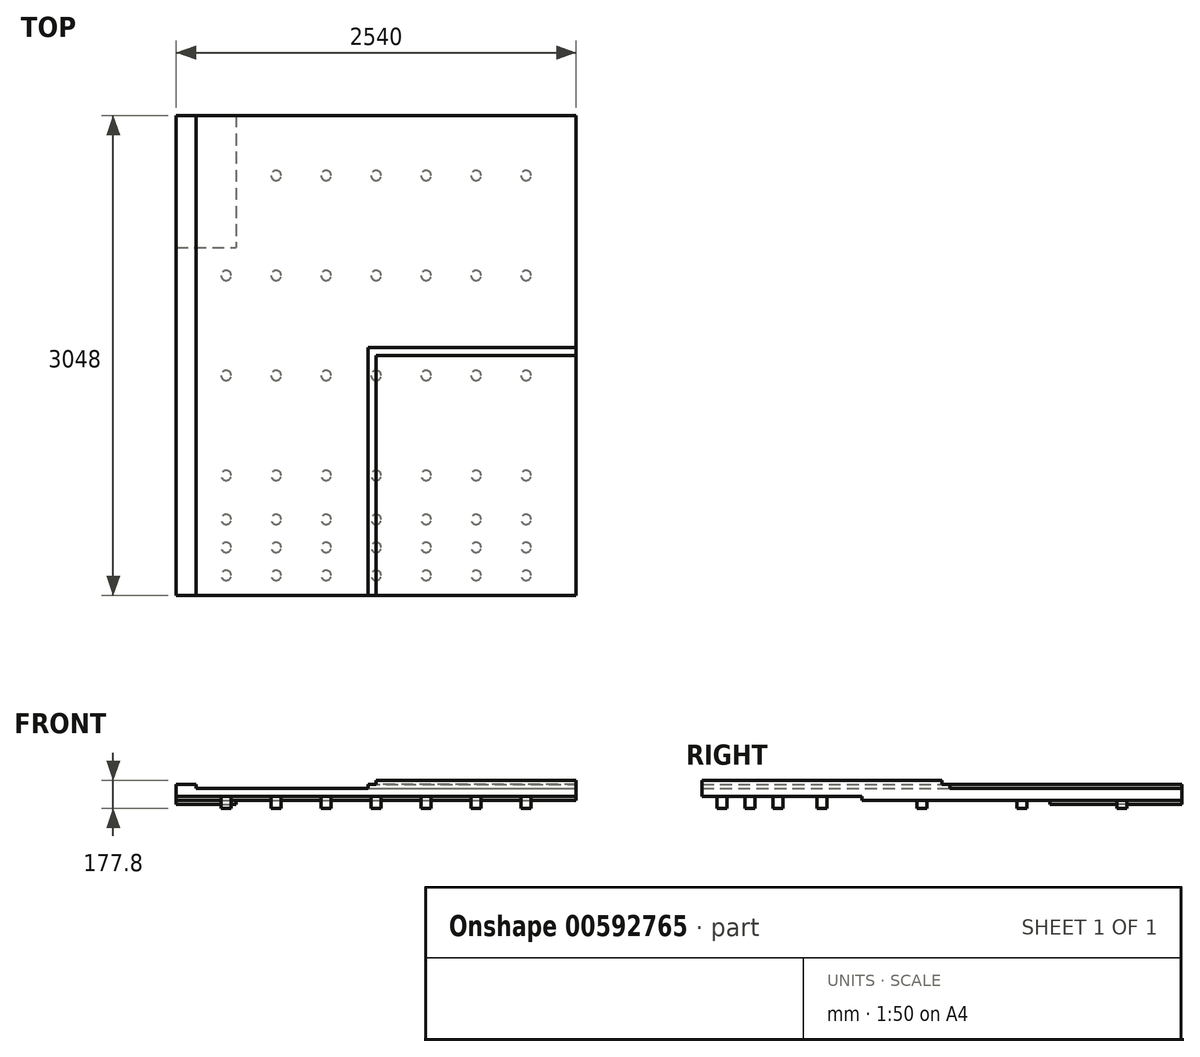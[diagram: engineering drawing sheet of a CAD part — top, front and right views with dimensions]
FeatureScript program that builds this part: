
annotation { "Feature Type Name" : "Feature", "Feature Type Description" : "" }
export const myFeature = defineFeature(function(context is Context, id is Id, definition is map)
    precondition{}
    {
        {
            var Q0;
            Q0=qCreatedBy(makeId("Top.planeOp"),FACE);
            var sketch = newSketch(context, id + "F0", { "sketchPlane" : qUnion([Q0])});
            skLineSegment(sketch, "E0.bottom", {"start": v(0, 0) * mm, "end": v(2540, 0) * mm});
            skLineSegment(sketch, "E0.top", {"start": v(0, 3048) * mm, "end": v(2540, 3048) * mm});
            skLineSegment(sketch, "E0.left", {"start": v(0, 0) * mm, "end": v(0, 3048) * mm});
            skLineSegment(sketch, "E0.right", {"start": v(2540, 0) * mm, "end": v(2540, 3048) * mm});
            skSolve(sketch);
        }
        {
            var Q0;
            Q0 = qSketchRegion(id + "F0", true);
            extrude(context, id + "F1", {"entities" : qUnion([Q0]), "depth" : 25.4 * mm, "offsetDistance" : 25.4 * mm});
        }
        {
            var Q0;
            Q0=makeQuery(id+"F1.opExtrude","CAP_FACE",FACE,{"disambiguationData":[OSD([sQuery(id+"F0.wireOp",EDGE,"E0.bottom"),sQuery(id+"F0.wireOp",EDGE,"E0.top"),sQuery(id+"F0.wireOp",EDGE,"E0.left"),sQuery(id+"F0.wireOp",EDGE,"E0.right")])],"isStart":false});
            extrude(context, id + "F2", {"entities" : qUnion([Q0]), "operationType" : NewBodyOperationType.ADD, "depth" : 25.4 * mm, "offsetDistance" : 25.4 * mm});
        }
        {
            var Q0;
            Q0=makeQuery(id+"F2.opExtrude","CAP_FACE",FACE,{"disambiguationData":[OSD([sQuery(id+"F0.wireOp",EDGE,"E0.bottom"),sQuery(id+"F0.wireOp",EDGE,"E0.top"),sQuery(id+"F0.wireOp",EDGE,"E0.left"),sQuery(id+"F0.wireOp",EDGE,"E0.right")])],"isStart":false});
            var sketch = newSketch(context, id + "F3", { "sketchPlane" : qUnion([Q0])});
            skLineSegment(sketch, "E1.bottom", {"start": v(1219.2, 0) * mm, "end": v(2540, 0) * mm});
            skLineSegment(sketch, "E1.top", {"start": v(1219.2, 1574.8) * mm, "end": v(2540, 1574.8) * mm});
            skLineSegment(sketch, "E1.left", {"start": v(1219.2, 0) * mm, "end": v(1219.2, 1574.8) * mm});
            skLineSegment(sketch, "E1.right", {"start": v(2540, 0) * mm, "end": v(2540, 1574.8) * mm});
            skLineSegment(sketch, "E2.bottom", {"start": v(0, 2032) * mm, "end": v(127, 2032) * mm});
            skLineSegment(sketch, "E2.top", {"start": v(0, 3048) * mm, "end": v(127, 3048) * mm});
            skLineSegment(sketch, "E2.left", {"start": v(0, 2032) * mm, "end": v(0, 3048) * mm});
            skLineSegment(sketch, "E2.right", {"start": v(127, 2032) * mm, "end": v(127, 3048) * mm});
            skLineSegment(sketch, "E3.bottom", {"start": v(0, 0) * mm, "end": v(127, 0) * mm});
            skLineSegment(sketch, "E3.left", {"start": v(0, 0) * mm, "end": v(0, 2032) * mm});
            skLineSegment(sketch, "E3.right", {"start": v(127, 0) * mm, "end": v(127, 2032) * mm});
            skSolve(sketch);
        }
        {
            var Q0;
            Q0=makeQuery(id+"F3.imprint","IMPRINT",FACE,{"disambiguationData":[TD([[makeQuery(id+"F3.imprint","IMPRINT",EDGE,{"derivedFrom":sQuery(id+"F3.wireOp",EDGE,"E2.top")}),-1.0]])]});
            var Q1;
            Q1=makeQuery(id+"F3.imprint","IMPRINT",FACE,{"disambiguationData":[TD([[makeQuery(id+"F3.imprint","IMPRINT",EDGE,{"derivedFrom":sQuery(id+"F3.wireOp",EDGE,"E3.bottom")}),1.0]])]});
            var Q2;
            Q2=makeQuery(id+"F3.imprint","IMPRINT",FACE,{"disambiguationData":[TD([[makeQuery(id+"F3.imprint","IMPRINT",EDGE,{"derivedFrom":sQuery(id+"F3.wireOp",EDGE,"E1.bottom")}),1.0]])]});
            extrude(context, id + "F4", {"entities" : qUnion([Q0, Q1, Q2]), "operationType" : NewBodyOperationType.ADD, "depth" : 25.4 * mm, "offsetDistance" : 25.4 * mm});
        }
        {
            var Q0;
            Q0=makeQuery(id+"F1.opExtrude","CAP_FACE",FACE,{"disambiguationData":[OSD([sQuery(id+"F0.wireOp",EDGE,"E0.bottom"),sQuery(id+"F0.wireOp",EDGE,"E0.top"),sQuery(id+"F0.wireOp",EDGE,"E0.left"),sQuery(id+"F0.wireOp",EDGE,"E0.right")])],"isStart":true});
            var sketch = newSketch(context, id + "F5", { "sketchPlane" : qUnion([Q0])});
            skLineSegment(sketch, "E4.bottom", {"start": v(0, -3048) * mm, "end": v(2540, -3048) * mm});
            skLineSegment(sketch, "E4.top", {"start": v(0, -1016) * mm, "end": v(2540, -1016) * mm});
            skLineSegment(sketch, "E4.left", {"start": v(0, -3048) * mm, "end": v(0, -1016) * mm});
            skLineSegment(sketch, "E4.right", {"start": v(2540, -3048) * mm, "end": v(2540, -1016) * mm});
            skSolve(sketch);
        }
        {
            var Q0;
            Q0 = qSketchRegion(id + "F5", true);
            var Q1;
            Q1=makeQuery(id+"F5.imprint","IMPRINT",FACE,{"disambiguationData":[TD([[makeQuery(id+"F5.imprint","IMPRINT",EDGE,{"derivedFrom":sQuery(id+"F5.wireOp",EDGE,"E4.bottom")}),1.0]])]});
            extrude(context, id + "F6", {"entities" : qUnion([Q0, Q1]), "operationType" : NewBodyOperationType.ADD, "depth" : 25.4 * mm, "offsetDistance" : 25.4 * mm});
        }
        {
            var Q0;
            Q0=makeQuery(id+"F6.opExtrude","CAP_FACE",FACE,{"disambiguationData":[OSD([sQuery(id+"F5.wireOp",EDGE,"E4.bottom"),sQuery(id+"F5.wireOp",EDGE,"E4.top"),sQuery(id+"F5.wireOp",EDGE,"E4.left"),sQuery(id+"F5.wireOp",EDGE,"E4.right")])],"isStart":false});
            var sketch = newSketch(context, id + "F7", { "sketchPlane" : qUnion([Q0])});
            skLineSegment(sketch, "E5.bottom", {"start": v(0, -3048) * mm, "end": v(381, -3048) * mm});
            skLineSegment(sketch, "E5.top", {"start": v(0, -2209.8) * mm, "end": v(381, -2209.8) * mm});
            skLineSegment(sketch, "E5.left", {"start": v(0, -3048) * mm, "end": v(0, -2209.8) * mm});
            skLineSegment(sketch, "E5.right", {"start": v(381, -3048) * mm, "end": v(381, -2209.8) * mm});
            skSolve(sketch);
        }
        {
            var Q0;
            Q0 = qSketchRegion(id + "F7", true);
            var Q1;
            Q1=makeQuery(id+"F7.imprint","IMPRINT",FACE,{"disambiguationData":[TD([[makeQuery(id+"F7.imprint","IMPRINT",EDGE,{"derivedFrom":sQuery(id+"F7.wireOp",EDGE,"E5.bottom")}),1.0]])]});
            extrude(context, id + "F8", {"entities" : qUnion([Q0, Q1]), "operationType" : NewBodyOperationType.ADD, "depth" : 25.4 * mm, "offsetDistance" : 25.4 * mm});
        }
        {
            var Q0;
            Q0=makeQuery(id+"F4.opExtrude","CAP_FACE",FACE,{"disambiguationData":[OSD([sQuery(id+"F3.wireOp",EDGE,"E1.bottom"),sQuery(id+"F3.wireOp",EDGE,"E1.top"),sQuery(id+"F3.wireOp",EDGE,"E1.left"),sQuery(id+"F3.wireOp",EDGE,"E1.right")])],"isStart":false});
            var sketch = newSketch(context, id + "F9", { "sketchPlane" : qUnion([Q0])});
            skLineSegment(sketch, "E6.bottom", {"start": v(2540, 0) * mm, "end": v(1270, 0) * mm});
            skLineSegment(sketch, "E6.top", {"start": v(2540, 1524) * mm, "end": v(1270, 1524) * mm});
            skLineSegment(sketch, "E6.left", {"start": v(2540, 0) * mm, "end": v(2540, 1524) * mm});
            skLineSegment(sketch, "E6.right", {"start": v(1270, 0) * mm, "end": v(1270, 1524) * mm});
            skSolve(sketch);
        }
        {
            var Q0;
            Q0=makeQuery(id+"F9.imprint","IMPRINT",FACE,{"disambiguationData":[TD([[makeQuery(id+"F9.imprint","IMPRINT",EDGE,{"derivedFrom":sQuery(id+"F9.wireOp",EDGE,"E6.bottom")}),1.0]])]});
            extrude(context, id + "F10", {"entities" : qUnion([Q0]), "operationType" : NewBodyOperationType.ADD, "depth" : 25.4 * mm, "offsetDistance" : 25.4 * mm});
        }
        {
            var Q0;
            Q0=qCreatedBy(makeId("Top.planeOp"),FACE);
            var sketch = newSketch(context, id + "F11", { "sketchPlane" : qUnion([Q0])});
            skCircle(sketch, "E7", {"center": v(2222.5, 2667) * mm, "radius": 31.75 * mm});
            skCircle(sketch, "E8.0.1.0", {"center": v(2222.5, 2032) * mm, "radius": 31.75 * mm});
            skCircle(sketch, "E8.0.2.0", {"center": v(2222.5, 1397) * mm, "radius": 31.75 * mm});
            skCircle(sketch, "E8.0.3.0", {"center": v(2222.5, 762) * mm, "radius": 31.75 * mm});
            skCircle(sketch, "E8.1.0.0", {"center": v(1905, 2667) * mm, "radius": 31.75 * mm});
            skCircle(sketch, "E8.1.1.0", {"center": v(1905, 2032) * mm, "radius": 31.75 * mm});
            skCircle(sketch, "E8.1.2.0", {"center": v(1905, 1397) * mm, "radius": 31.75 * mm});
            skCircle(sketch, "E8.1.3.0", {"center": v(1905, 762) * mm, "radius": 31.75 * mm});
            skCircle(sketch, "E8.2.0.0", {"center": v(1587.5, 2667) * mm, "radius": 31.75 * mm});
            skCircle(sketch, "E8.2.1.0", {"center": v(1587.5, 2032) * mm, "radius": 31.75 * mm});
            skCircle(sketch, "E8.2.2.0", {"center": v(1587.5, 1397) * mm, "radius": 31.75 * mm});
            skCircle(sketch, "E8.2.3.0", {"center": v(1587.5, 762) * mm, "radius": 31.75 * mm});
            skCircle(sketch, "E8.3.0.0", {"center": v(1270, 2667) * mm, "radius": 31.75 * mm});
            skCircle(sketch, "E8.3.1.0", {"center": v(1270, 2032) * mm, "radius": 31.75 * mm});
            skCircle(sketch, "E8.3.2.0", {"center": v(1270, 1397) * mm, "radius": 31.75 * mm});
            skCircle(sketch, "E8.3.3.0", {"center": v(1270, 762) * mm, "radius": 31.75 * mm});
            skCircle(sketch, "E8.4.0.0", {"center": v(952.5, 2667) * mm, "radius": 31.75 * mm});
            skCircle(sketch, "E8.4.1.0", {"center": v(952.5, 2032) * mm, "radius": 31.75 * mm});
            skCircle(sketch, "E8.4.2.0", {"center": v(952.5, 1397) * mm, "radius": 31.75 * mm});
            skCircle(sketch, "E8.4.3.0", {"center": v(952.5, 762) * mm, "radius": 31.75 * mm});
            skCircle(sketch, "E8.5.0.0", {"center": v(635, 2667) * mm, "radius": 31.75 * mm});
            skCircle(sketch, "E8.5.1.0", {"center": v(635, 2032) * mm, "radius": 31.75 * mm});
            skCircle(sketch, "E8.5.2.0", {"center": v(635, 1397) * mm, "radius": 31.75 * mm});
            skCircle(sketch, "E8.5.3.0", {"center": v(635, 762) * mm, "radius": 31.75 * mm});
            skCircle(sketch, "E8.6.1.0", {"center": v(317.5, 2032) * mm, "radius": 31.75 * mm});
            skCircle(sketch, "E8.6.2.0", {"center": v(317.5, 1397) * mm, "radius": 31.75 * mm});
            skCircle(sketch, "E8.6.3.0", {"center": v(317.5, 762) * mm, "radius": 31.75 * mm});
            skLineSegment(sketch, "E8.direction1", {"start": v(2222.5, 2667) * mm, "end": v(1905, 2667) * mm, "construction": true});
            skLineSegment(sketch, "E8.direction2", {"start": v(2222.5, 2667) * mm, "end": v(2222.5, 2032) * mm, "construction": true});
            skCircle(sketch, "E9", {"center": v(317.5, 127) * mm, "radius": 31.75 * mm});
            skCircle(sketch, "E10.0.1.0", {"center": v(317.5, 304.8) * mm, "radius": 31.75 * mm});
            skCircle(sketch, "E10.0.2.0", {"center": v(317.5, 482.6) * mm, "radius": 31.75 * mm});
            skCircle(sketch, "E10.1.0.0", {"center": v(635, 127) * mm, "radius": 31.75 * mm});
            skCircle(sketch, "E10.1.1.0", {"center": v(635, 304.8) * mm, "radius": 31.75 * mm});
            skCircle(sketch, "E10.1.2.0", {"center": v(635, 482.6) * mm, "radius": 31.75 * mm});
            skCircle(sketch, "E10.2.0.0", {"center": v(952.5, 127) * mm, "radius": 31.75 * mm});
            skCircle(sketch, "E10.2.1.0", {"center": v(952.5, 304.8) * mm, "radius": 31.75 * mm});
            skCircle(sketch, "E10.2.2.0", {"center": v(952.5, 482.6) * mm, "radius": 31.75 * mm});
            skCircle(sketch, "E10.3.0.0", {"center": v(1270, 127) * mm, "radius": 31.75 * mm});
            skCircle(sketch, "E10.3.1.0", {"center": v(1270, 304.8) * mm, "radius": 31.75 * mm});
            skCircle(sketch, "E10.3.2.0", {"center": v(1270, 482.6) * mm, "radius": 31.75 * mm});
            skCircle(sketch, "E10.4.0.0", {"center": v(1587.5, 127) * mm, "radius": 31.75 * mm});
            skCircle(sketch, "E10.4.1.0", {"center": v(1587.5, 304.8) * mm, "radius": 31.75 * mm});
            skCircle(sketch, "E10.4.2.0", {"center": v(1587.5, 482.6) * mm, "radius": 31.75 * mm});
            skCircle(sketch, "E10.5.0.0", {"center": v(1905, 127) * mm, "radius": 31.75 * mm});
            skCircle(sketch, "E10.5.1.0", {"center": v(1905, 304.8) * mm, "radius": 31.75 * mm});
            skCircle(sketch, "E10.5.2.0", {"center": v(1905, 482.6) * mm, "radius": 31.75 * mm});
            skCircle(sketch, "E10.6.0.0", {"center": v(2222.5, 127) * mm, "radius": 31.75 * mm});
            skCircle(sketch, "E10.6.1.0", {"center": v(2222.5, 304.8) * mm, "radius": 31.75 * mm});
            skCircle(sketch, "E10.6.2.0", {"center": v(2222.5, 482.6) * mm, "radius": 31.75 * mm});
            skLineSegment(sketch, "E10.direction1", {"start": v(317.5, 127) * mm, "end": v(635, 127) * mm, "construction": true});
            skLineSegment(sketch, "E10.direction2", {"start": v(317.5, 127) * mm, "end": v(317.5, 304.8) * mm, "construction": true});
            skSolve(sketch);
        }
        {
            var Q0;
            Q0 = qSketchRegion(id + "F11", true);
            extrude(context, id + "F12", {"entities" : qUnion([Q0]), "operationType" : NewBodyOperationType.ADD, "oppositeDirection" : true, "depth" : 76.2 * mm, "offsetDistance" : 25.4 * mm});
        }
    });
